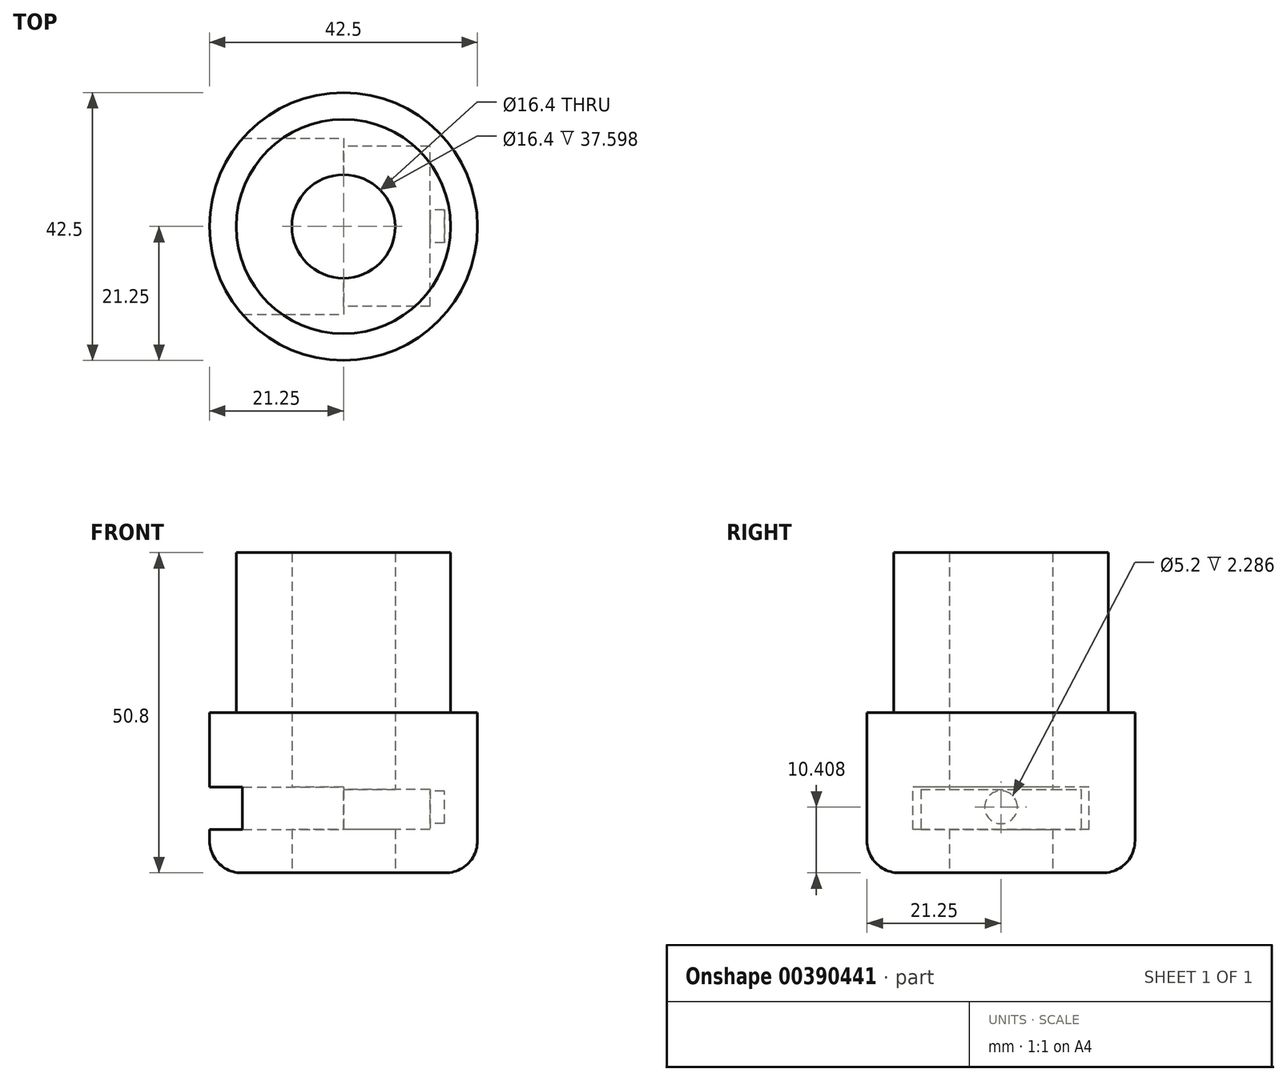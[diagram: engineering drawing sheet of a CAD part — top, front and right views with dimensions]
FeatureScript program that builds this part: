
annotation { "Feature Type Name" : "Feature", "Feature Type Description" : "" }
export const myFeature = defineFeature(function(context is Context, id is Id, definition is map)
    precondition{}
    {
        {
            var Q0;
            Q0=qCreatedBy(makeId("Top.planeOp"),FACE);
            var sketch = newSketch(context, id + "F0", { "sketchPlane" : qUnion([Q0])});
            skCircle(sketch, "E0", {"center": v(0, 0) * mm, "radius": 17 * mm});
            skSolve(sketch);
        }
        {
            var Q0;
            Q0 = qSketchRegion(id + "F0", true);
            extrude(context, id + "F1", {"entities" : qUnion([Q0]), "depth" : 25.4 * mm});
        }
        {
            var Q0;
            Q0=qCreatedBy(makeId("Top.planeOp"),FACE);
            var sketch = newSketch(context, id + "F2", { "sketchPlane" : qUnion([Q0])});
            skCircle(sketch, "E1", {"center": v(0, 0) * mm, "radius": 21.25 * mm});
            skSolve(sketch);
        }
        {
            var Q0;
            Q0 = qSketchRegion(id + "F2", true);
            extrude(context, id + "F3", {"entities" : qUnion([Q0]), "operationType" : NewBodyOperationType.ADD, "oppositeDirection" : true, "depth" : 25.4 * mm});
        }
        {
            var Q0;
            Q0=makeQuery(id+"F3.opExtrude","CAP_FACE",FACE,{"disambiguationData":[OSD([sQuery(id+"F2.wireOp",EDGE,"E1")])],"isStart":false});
            var sketch = newSketch(context, id + "F4", { "sketchPlane" : qUnion([Q0])});
            skCircle(sketch, "E2", {"center": v(0, 0) * mm, "radius": 8.2 * mm});
            skSolve(sketch);
        }
        {
            var Q0;
            Q0 = qSketchRegion(id + "F4", true);
            extrude(context, id + "F5", {"entities" : qUnion([Q0]), "operationType" : NewBodyOperationType.REMOVE, "oppositeDirection" : true, "depth" : 87.88 * mm});
        }
        {
            var Q0;
            Q0=qCreatedBy(makeId("Right.planeOp"),FACE);
            var sketch = newSketch(context, id + "F6", { "sketchPlane" : qUnion([Q0])});
            skLineSegment(sketch, "E3.bottom", {"start": v(13.97, -18.55) * mm, "end": v(-13.97, -18.55) * mm});
            skLineSegment(sketch, "E3.top", {"start": v(13.97, -11.82) * mm, "end": v(-13.97, -11.82) * mm});
            skLineSegment(sketch, "E3.left", {"start": v(13.97, -18.55) * mm, "end": v(13.97, -11.82) * mm});
            skLineSegment(sketch, "E3.right", {"start": v(-13.97, -18.55) * mm, "end": v(-13.97, -11.82) * mm});
            skPoint(sketch, "E3.middle", {"position": v(0, -15.18) * mm});
            skSolve(sketch);
        }
        {
            var Q0;
            Q0 = qSketchRegion(id + "F6", true);
            extrude(context, id + "F7", {"entities" : qUnion([Q0]), "operationType" : NewBodyOperationType.REMOVE, "oppositeDirection" : true, "depth" : 25.4 * mm});
        }
        {
            var Q0;
            Q0=qCreatedBy(makeId("Right.planeOp"),FACE);
            var sketch = newSketch(context, id + "F8", { "sketchPlane" : qUnion([Q0])});
            skCircle(sketch, "E4", {"center": v(0, -15) * mm, "radius": 2.6 * mm});
            skSolve(sketch);
        }
        {
            var Q0;
            Q0 = qSketchRegion(id + "F8", true);
            extrude(context, id + "F9", {"entities" : qUnion([Q0]), "operationType" : NewBodyOperationType.REMOVE, "depth" : 16 * mm});
        }
        {
            var Q0;
            Q0=qCreatedBy(makeId("Right.planeOp"),FACE);
            var sketch = newSketch(context, id + "F10", { "sketchPlane" : qUnion([Q0])});
            skLineSegment(sketch, "E5.bottom", {"start": v(-12.7, -12.2) * mm, "end": v(12.7, -12.2) * mm});
            skLineSegment(sketch, "E5.top", {"start": v(-12.7, -18.55) * mm, "end": v(12.7, -18.55) * mm});
            skLineSegment(sketch, "E5.left", {"start": v(-12.7, -12.2) * mm, "end": v(-12.7, -18.55) * mm});
            skLineSegment(sketch, "E5.right", {"start": v(12.7, -12.2) * mm, "end": v(12.7, -18.55) * mm});
            skPoint(sketch, "E5.middle", {"position": v(0, -15.37) * mm});
            skSolve(sketch);
        }
        {
            var Q0;
            Q0 = qSketchRegion(id + "F10", true);
            extrude(context, id + "F11", {"entities" : qUnion([Q0]), "operationType" : NewBodyOperationType.REMOVE, "depth" : 13.72 * mm});
        }
        {
            var Q0;
            Q0=makeQuery(id+"F3.opExtrude","CAP_EDGE",EDGE,{"disambiguationData":[OSD([sQuery(id+"F2.wireOp",EDGE,"E1")])],"isStart":false});
            fillet(context, id + "F12", {"entities" : qUnion([Q0]), "radius" : 5.08 * mm, "tangentPropagation" : true, "allowEdgeOverflow" : false});
        }
    });
